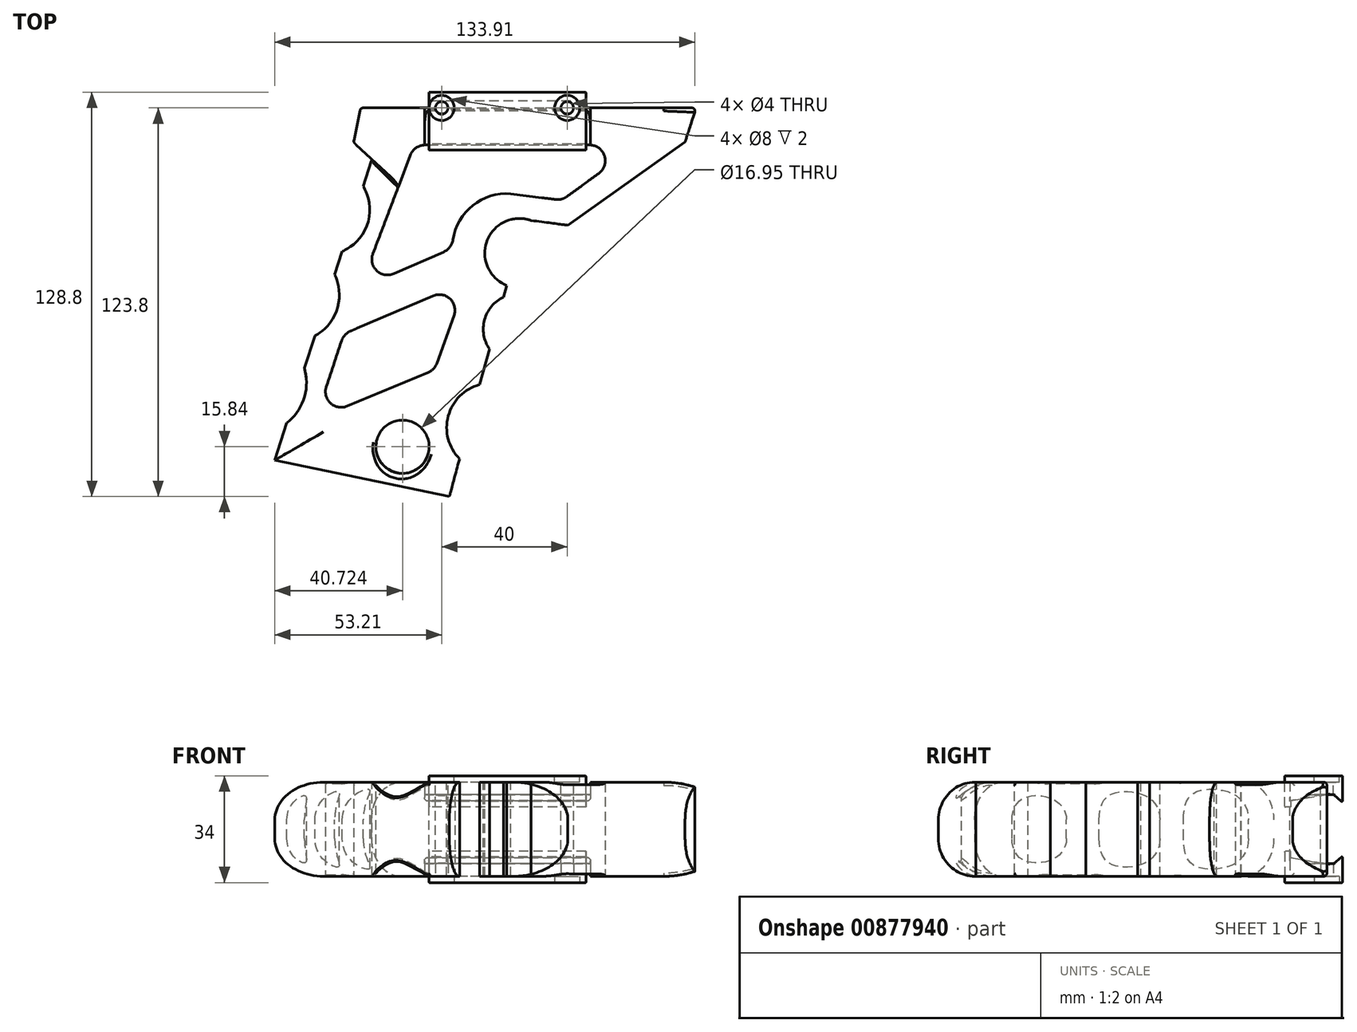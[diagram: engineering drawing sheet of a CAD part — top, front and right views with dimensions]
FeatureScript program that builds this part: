
annotation { "Feature Type Name" : "Feature", "Feature Type Description" : "" }
export const myFeature = defineFeature(function(context is Context, id is Id, definition is map)
    precondition{}
    {
        {
            var Q0;
            Q0=qCreatedBy(makeId("Top.planeOp"),FACE);
            var sketch = newSketch(context, id + "F0", { "sketchPlane" : qUnion([Q0])});
            skLineSegment(sketch, "E0", {"start": v(-36.24, 0) * mm, "end": v(-38.5, -10.92) * mm});
            skLineSegment(sketch, "E1", {"start": v(-38.5, -10.92) * mm, "end": v(-32.62, -16.35) * mm});
            skLineSegment(sketch, "E2", {"start": v(-32.62, -16.35) * mm, "end": v(-63.6, -112.26) * mm});
            skLineSegment(sketch, "E3", {"start": v(-63.6, -112.26) * mm, "end": v(-7.96, -123.8) * mm});
            skLineSegment(sketch, "E4", {"start": v(-7.96, -123.8) * mm, "end": v(16.02, -35.58) * mm});
            skLineSegment(sketch, "E5", {"start": v(16.02, -35.58) * mm, "end": v(29.82, -37.39) * mm});
            skLineSegment(sketch, "E6", {"start": v(29.82, -37.39) * mm, "end": v(67.14, -10.92) * mm});
            skLineSegment(sketch, "E7", {"start": v(67.14, -10.92) * mm, "end": v(70.67, 0) * mm});
            skLineSegment(sketch, "E8", {"start": v(-36.24, 0) * mm, "end": v(70.67, 0) * mm});
            skPoint(sketch, "E9.first.point", {"position": v(-35.48, -25.23) * mm});
            skPoint(sketch, "E9.second.point", {"position": v(-42.4, -46.63) * mm});
            skPoint(sketch, "E9.third.point", {"position": v(-65.03, -33.08) * mm});
            skPoint(sketch, "E10.first.point", {"position": v(-44.67, -53.65) * mm});
            skPoint(sketch, "E10.second.point", {"position": v(-50.9, -72.91) * mm});
            skPoint(sketch, "E10.third.point", {"position": v(-72.52, -56.97) * mm});
            skPoint(sketch, "E11.first.point", {"position": v(-54.13, -82.94) * mm});
            skPoint(sketch, "E11.second.point", {"position": v(-59.89, -100.75) * mm});
            skPoint(sketch, "E11.third.point", {"position": v(-85, -82.64) * mm});
            skLineSegment(sketch, "E12", {"start": v(-97.37, -25.23) * mm, "end": v(-7.02, -25.23) * mm, "construction": true});
            skLineSegment(sketch, "E13", {"start": v(-95.85, -46.63) * mm, "end": v(-7.4, -46.63) * mm, "construction": true});
            skLineSegment(sketch, "E14", {"start": v(-81.01, -53.65) * mm, "end": v(-12.15, -53.65) * mm, "construction": true});
            skLineSegment(sketch, "E15", {"start": v(-92.8, -72.91) * mm, "end": v(-15.2, -72.91) * mm, "construction": true});
            skLineSegment(sketch, "E16", {"start": v(-54.13, -82.94) * mm, "end": v(-73.21, -82.94) * mm});
            skLineSegment(sketch, "E17", {"start": v(-73.21, -82.94) * mm, "end": v(-28.9, -82.94) * mm, "construction": true});
            skLineSegment(sketch, "E18", {"start": v(-59.89, -100.75) * mm, "end": v(-91.1, -100.75) * mm});
            skLineSegment(sketch, "E19", {"start": v(-91.1, -100.75) * mm, "end": v(-23.57, -100.75) * mm, "construction": true});
            skLineSegment(sketch, "E20", {"start": v(-30.41, -25.23) * mm, "end": v(-60.21, -112.97) * mm, "construction": true});
            skSolve(sketch);
        }
        {
            var Q0;
            Q0 = qSketchRegion(id + "F0", true);
            extrude(context, id + "F1", {"entities" : qUnion([Q0]), "endBound" : BoundingType.SYMMETRIC, "depth" : 30 * mm, "offsetDistance" : 25 * mm});
        }
        {
            var Q0;
            Q0=qCreatedBy(makeId("Top.planeOp"),FACE);
            var sketch = newSketch(context, id + "F2", { "sketchPlane" : qUnion([Q0])});
            skCircle(sketch, "E21", {"center": v(-47.66, -32.46) * mm, "radius": 14.36 * mm});
            skPoint(sketch, "E21.first.point", {"position": v(-35.59, -24.68) * mm});
            skPoint(sketch, "E21.second.point", {"position": v(-43.3, -46.15) * mm});
            skPoint(sketch, "E21.third.point", {"position": v(-61.39, -28.25) * mm});
            skCircle(sketch, "E22", {"center": v(-57.68, -59.62) * mm, "radius": 14.67 * mm});
            skPoint(sketch, "E22.first.point", {"position": v(-44.44, -53.3) * mm});
            skPoint(sketch, "E22.second.point", {"position": v(-51.03, -72.7) * mm});
            skPoint(sketch, "E22.third.point", {"position": v(-72.31, -58.58) * mm});
            skCircle(sketch, "E23", {"center": v(-69.65, -87.55) * mm, "radius": 16.16 * mm});
            skPoint(sketch, "E23.first.point", {"position": v(-54.23, -82.68) * mm});
            skPoint(sketch, "E23.second.point", {"position": v(-60.07, -100.57) * mm});
            skPoint(sketch, "E23.third.point", {"position": v(-85.5, -84.38) * mm});
            skCircle(sketch, "E24", {"center": v(-22.89, -107.96) * mm, "radius": 8.48 * mm});
            skPoint(sketch, "E24.first.point", {"position": v(-24.85, -116.2) * mm});
            skPoint(sketch, "E24.second.point", {"position": v(-20.52, -99.82) * mm});
            skPoint(sketch, "E24.third.point", {"position": v(-15.62, -103.59) * mm});
            skCircle(sketch, "E25", {"center": v(14.39, -46.27) * mm, "radius": 11.05 * mm});
            skPoint(sketch, "E25.first.point", {"position": v(16.03, -35.34) * mm});
            skPoint(sketch, "E25.second.point", {"position": v(10.2, -56.5) * mm});
            skPoint(sketch, "E25.third.point", {"position": v(23.76, -52.13) * mm});
            skCircle(sketch, "E26", {"center": v(14.16, -70.47) * mm, "radius": 11.31 * mm});
            skPoint(sketch, "E26.first.point", {"position": v(9.42, -60.2) * mm});
            skPoint(sketch, "E26.second.point", {"position": v(5.17, -77.33) * mm});
            skPoint(sketch, "E26.third.point", {"position": v(24.99, -73.75) * mm});
            skCircle(sketch, "E27", {"center": v(5.4, -101.86) * mm, "radius": 14.2 * mm});
            skPoint(sketch, "E27.first.point", {"position": v(2, -88.08) * mm});
            skPoint(sketch, "E27.second.point", {"position": v(-4.5, -112.05) * mm});
            skPoint(sketch, "E27.third.point", {"position": v(18.9, -106.22) * mm});
            skSolve(sketch);
        }
        {
            var Q0;
            Q0 = qSketchRegion(id + "F2", true);
            extrude(context, id + "F3", {"entities" : qUnion([Q0]), "operationType" : NewBodyOperationType.REMOVE, "endBound" : BoundingType.SYMMETRIC, "oppositeDirection" : true, "depth" : 30 * mm, "offsetDistance" : 25 * mm});
        }
        {
            var Q0;
            {var subQ0=sQuery(id+"F2.wireOp",EDGE,"E22");Q0=makeQuery(id+"F3.boolean.opBoolean","COPY",EDGE,{"derivedFrom":makeQuery(id+"F3.opExtrude","CAP_EDGE",EDGE,{"disambiguationData":[OSD([subQ0]),TDD([makeQuery(id+"F2.imprint","IMPRINT",EDGE,{"disambiguationData":[TD([[makeQuery(id+"F2.imprint","INTERSECT",VERTEX,{"disambiguationData":[OD(1.0)],"derivedFrom":[sQuery(id+"F2.wireOp",EDGE,"E21"),subQ0]}),1.0]])],"derivedFrom":subQ0})])],"isStart":true})});}
            var Q1;
            Q1=makeQuery(id+"F3.boolean.opBoolean","COPY",EDGE,{"derivedFrom":makeQuery(id+"F3.opExtrude","CAP_EDGE",EDGE,{"disambiguationData":[OSD([sQuery(id+"F2.wireOp",EDGE,"E21")])],"isStart":true})});
            var Q2;
            Q2=makeQuery(id+"F3.boolean.opBoolean","COPY",EDGE,{"derivedFrom":makeQuery(id+"F3.opExtrude","CAP_EDGE",EDGE,{"disambiguationData":[OSD([sQuery(id+"F2.wireOp",EDGE,"E23")])],"isStart":true})});
            var Q3;
            Q3=makeQuery(id+"F3.boolean.opBoolean","COPY",EDGE,{"derivedFrom":makeQuery(id+"F3.opExtrude","CAP_EDGE",EDGE,{"disambiguationData":[OSD([sQuery(id+"F2.wireOp",EDGE,"E21")])],"isStart":false})});
            var Q4;
            {var subQ0=sQuery(id+"F2.wireOp",EDGE,"E22");Q4=makeQuery(id+"F3.boolean.opBoolean","COPY",EDGE,{"derivedFrom":makeQuery(id+"F3.opExtrude","CAP_EDGE",EDGE,{"disambiguationData":[OSD([subQ0]),TDD([makeQuery(id+"F2.imprint","IMPRINT",EDGE,{"disambiguationData":[TD([[makeQuery(id+"F2.imprint","INTERSECT",VERTEX,{"disambiguationData":[OD(1.0)],"derivedFrom":[sQuery(id+"F2.wireOp",EDGE,"E21"),subQ0]}),1.0]])],"derivedFrom":subQ0})])],"isStart":false})});}
            var Q5;
            Q5=makeQuery(id+"F3.boolean.opBoolean","COPY",EDGE,{"derivedFrom":makeQuery(id+"F3.opExtrude","CAP_EDGE",EDGE,{"disambiguationData":[OSD([sQuery(id+"F2.wireOp",EDGE,"E23")])],"isStart":false})});
            var Q6;
            {var subQ0=sQuery(id+"F0.wireOp",EDGE,"E2");var subQ1=sQuery(id+"F2.wireOp",EDGE,"E22");var subQ2=sQuery(id+"F2.wireOp",EDGE,"E23");Q6=makeQuery(id+"F3.boolean.opBoolean","SPLIT",EDGE,{"disambiguationData":[TD([makeQuery(id+"F1.opExtrude","CAP_FACE",FACE,{"disambiguationData":[OSD([sQuery(id+"F0.wireOp",EDGE,"E0"),sQuery(id+"F0.wireOp",EDGE,"E1"),subQ0,sQuery(id+"F0.wireOp",EDGE,"E3"),sQuery(id+"F0.wireOp",EDGE,"E4"),sQuery(id+"F0.wireOp",EDGE,"E5"),sQuery(id+"F0.wireOp",EDGE,"E6"),sQuery(id+"F0.wireOp",EDGE,"E7"),sQuery(id+"F0.wireOp",EDGE,"E8")])],"isStart":false}),makeQuery(id+"F1.opExtrude","SWEPT_FACE",FACE,{"disambiguationData":[OSD([subQ0])]}),makeQuery(id+"F3.opExtrude","SWEPT_FACE",FACE,{"disambiguationData":[OSD([subQ1]),TDD([makeQuery(id+"F2.imprint","IMPRINT",EDGE,{"disambiguationData":[TD([[makeQuery(id+"F2.imprint","INTERSECT",VERTEX,{"disambiguationData":[OD(1.0)],"derivedFrom":[sQuery(id+"F2.wireOp",EDGE,"E21"),subQ1]}),1.0]])],"derivedFrom":subQ1})])]}),makeQuery(id+"F3.opExtrude","SWEPT_FACE",FACE,{"disambiguationData":[OSD([subQ2])]})])],"derivedFrom":makeQuery(id+"F1.opExtrude","CAP_EDGE",EDGE,{"disambiguationData":[OSD([subQ0])],"isStart":false})});}
            var Q7;
            {var subQ0=sQuery(id+"F0.wireOp",EDGE,"E2");var subQ1=sQuery(id+"F2.wireOp",EDGE,"E22");var subQ2=sQuery(id+"F2.wireOp",EDGE,"E21");Q7=makeQuery(id+"F3.boolean.opBoolean","SPLIT",EDGE,{"disambiguationData":[TD([makeQuery(id+"F1.opExtrude","CAP_FACE",FACE,{"disambiguationData":[OSD([sQuery(id+"F0.wireOp",EDGE,"E0"),sQuery(id+"F0.wireOp",EDGE,"E1"),subQ0,sQuery(id+"F0.wireOp",EDGE,"E3"),sQuery(id+"F0.wireOp",EDGE,"E4"),sQuery(id+"F0.wireOp",EDGE,"E5"),sQuery(id+"F0.wireOp",EDGE,"E6"),sQuery(id+"F0.wireOp",EDGE,"E7"),sQuery(id+"F0.wireOp",EDGE,"E8")])],"isStart":false}),makeQuery(id+"F1.opExtrude","SWEPT_FACE",FACE,{"disambiguationData":[OSD([subQ0])]}),makeQuery(id+"F3.opExtrude","SWEPT_FACE",FACE,{"disambiguationData":[OSD([subQ2])]}),makeQuery(id+"F3.opExtrude","SWEPT_FACE",FACE,{"disambiguationData":[OSD([subQ1]),TDD([makeQuery(id+"F2.imprint","IMPRINT",EDGE,{"disambiguationData":[TD([[makeQuery(id+"F2.imprint","INTERSECT",VERTEX,{"disambiguationData":[OD(1.0)],"derivedFrom":[subQ2,subQ1]}),1.0]])],"derivedFrom":subQ1})])]})])],"derivedFrom":makeQuery(id+"F1.opExtrude","CAP_EDGE",EDGE,{"disambiguationData":[OSD([subQ0])],"isStart":false})});}
            var Q8;
            {var subQ0=sQuery(id+"F0.wireOp",EDGE,"E2");var subQ1=sQuery(id+"F2.wireOp",EDGE,"E22");var subQ2=sQuery(id+"F2.wireOp",EDGE,"E23");Q8=makeQuery(id+"F3.boolean.opBoolean","SPLIT",EDGE,{"disambiguationData":[TD([makeQuery(id+"F1.opExtrude","CAP_FACE",FACE,{"disambiguationData":[OSD([sQuery(id+"F0.wireOp",EDGE,"E0"),sQuery(id+"F0.wireOp",EDGE,"E1"),subQ0,sQuery(id+"F0.wireOp",EDGE,"E3"),sQuery(id+"F0.wireOp",EDGE,"E4"),sQuery(id+"F0.wireOp",EDGE,"E5"),sQuery(id+"F0.wireOp",EDGE,"E6"),sQuery(id+"F0.wireOp",EDGE,"E7"),sQuery(id+"F0.wireOp",EDGE,"E8")])],"isStart":true}),makeQuery(id+"F1.opExtrude","SWEPT_FACE",FACE,{"disambiguationData":[OSD([subQ0])]}),makeQuery(id+"F3.opExtrude","SWEPT_FACE",FACE,{"disambiguationData":[OSD([subQ1]),TDD([makeQuery(id+"F2.imprint","IMPRINT",EDGE,{"disambiguationData":[TD([[makeQuery(id+"F2.imprint","INTERSECT",VERTEX,{"disambiguationData":[OD(1.0)],"derivedFrom":[sQuery(id+"F2.wireOp",EDGE,"E21"),subQ1]}),1.0]])],"derivedFrom":subQ1})])]}),makeQuery(id+"F3.opExtrude","SWEPT_FACE",FACE,{"disambiguationData":[OSD([subQ2])]})])],"derivedFrom":makeQuery(id+"F1.opExtrude","CAP_EDGE",EDGE,{"disambiguationData":[OSD([subQ0])],"isStart":true})});}
            var Q9;
            {var subQ0=sQuery(id+"F0.wireOp",EDGE,"E2");var subQ1=sQuery(id+"F2.wireOp",EDGE,"E21");var subQ2=sQuery(id+"F2.wireOp",EDGE,"E22");Q9=makeQuery(id+"F3.boolean.opBoolean","SPLIT",EDGE,{"disambiguationData":[TD([makeQuery(id+"F1.opExtrude","CAP_FACE",FACE,{"disambiguationData":[OSD([sQuery(id+"F0.wireOp",EDGE,"E0"),sQuery(id+"F0.wireOp",EDGE,"E1"),subQ0,sQuery(id+"F0.wireOp",EDGE,"E3"),sQuery(id+"F0.wireOp",EDGE,"E4"),sQuery(id+"F0.wireOp",EDGE,"E5"),sQuery(id+"F0.wireOp",EDGE,"E6"),sQuery(id+"F0.wireOp",EDGE,"E7"),sQuery(id+"F0.wireOp",EDGE,"E8")])],"isStart":true}),makeQuery(id+"F1.opExtrude","SWEPT_FACE",FACE,{"disambiguationData":[OSD([subQ0])]}),makeQuery(id+"F3.opExtrude","SWEPT_FACE",FACE,{"disambiguationData":[OSD([subQ1])]}),makeQuery(id+"F3.opExtrude","SWEPT_FACE",FACE,{"disambiguationData":[OSD([subQ2]),TDD([makeQuery(id+"F2.imprint","IMPRINT",EDGE,{"disambiguationData":[TD([[makeQuery(id+"F2.imprint","INTERSECT",VERTEX,{"disambiguationData":[OD(1.0)],"derivedFrom":[subQ1,subQ2]}),1.0]])],"derivedFrom":subQ2})])]})])],"derivedFrom":makeQuery(id+"F1.opExtrude","CAP_EDGE",EDGE,{"disambiguationData":[OSD([subQ0])],"isStart":true})});}
            var Q10;
            Q10=makeQuery(id+"F3.boolean.opBoolean","COPY",EDGE,{"derivedFrom":makeQuery(id+"F3.opExtrude","CAP_EDGE",EDGE,{"disambiguationData":[OSD([sQuery(id+"F2.wireOp",EDGE,"E25")])],"isStart":true})});
            var Q11;
            Q11=makeQuery(id+"F3.boolean.opBoolean","COPY",EDGE,{"derivedFrom":makeQuery(id+"F3.opExtrude","CAP_EDGE",EDGE,{"disambiguationData":[OSD([sQuery(id+"F2.wireOp",EDGE,"E26")])],"isStart":true})});
            var Q12;
            Q12=makeQuery(id+"F3.boolean.opBoolean","COPY",EDGE,{"derivedFrom":makeQuery(id+"F3.opExtrude","CAP_EDGE",EDGE,{"disambiguationData":[OSD([sQuery(id+"F2.wireOp",EDGE,"E27")])],"isStart":true})});
            var Q13;
            Q13=makeQuery(id+"F3.boolean.opBoolean","COPY",EDGE,{"derivedFrom":makeQuery(id+"F3.opExtrude","CAP_EDGE",EDGE,{"disambiguationData":[OSD([sQuery(id+"F2.wireOp",EDGE,"E27")])],"isStart":false})});
            var Q14;
            Q14=makeQuery(id+"F3.boolean.opBoolean","COPY",EDGE,{"derivedFrom":makeQuery(id+"F3.opExtrude","CAP_EDGE",EDGE,{"disambiguationData":[OSD([sQuery(id+"F2.wireOp",EDGE,"E26")])],"isStart":false})});
            var Q15;
            Q15=makeQuery(id+"F3.boolean.opBoolean","COPY",EDGE,{"derivedFrom":makeQuery(id+"F3.opExtrude","CAP_EDGE",EDGE,{"disambiguationData":[OSD([sQuery(id+"F2.wireOp",EDGE,"E25")])],"isStart":false})});
            var Q16;
            Q16=makeQuery(id+"F1.opExtrude","CAP_EDGE",EDGE,{"disambiguationData":[OSD([sQuery(id+"F0.wireOp",EDGE,"E6")])],"isStart":true});
            var Q17;
            Q17=makeQuery(id+"F1.opExtrude","CAP_EDGE",EDGE,{"disambiguationData":[OSD([sQuery(id+"F0.wireOp",EDGE,"E6")])],"isStart":false});
            var Q18;
            Q18=makeQuery(id+"F1.opExtrude","CAP_EDGE",EDGE,{"disambiguationData":[OSD([sQuery(id+"F0.wireOp",EDGE,"E3")])],"isStart":true});
            var Q19;
            Q19=makeQuery(id+"F1.opExtrude","CAP_EDGE",EDGE,{"disambiguationData":[OSD([sQuery(id+"F0.wireOp",EDGE,"E3")])],"isStart":false});
            fillet(context, id + "F4", {"entities" : qUnion([Q0, Q1, Q2, Q3, Q4, Q5, Q6, Q7, Q8, Q9, Q10, Q11, Q12, Q13, Q14, Q15, Q16, Q17, Q18, Q19]), "radius" : 12 * mm, "tangentPropagation" : true, "allowEdgeOverflow" : false});
        }
        {
            var Q0;
            Q0=makeQuery(id+"F1.opExtrude","SWEPT_EDGE",EDGE,{"disambiguationData":[OSD([sQuery(id+"F0.wireOp",EDGE,"E1"),sQuery(id+"F0.wireOp",EDGE,"E2")])]});
            var Q1;
            Q1=makeQuery(id+"F1.opExtrude","SWEPT_EDGE",EDGE,{"disambiguationData":[OSD([sQuery(id+"F0.wireOp",EDGE,"E0"),sQuery(id+"F0.wireOp",EDGE,"E1")])]});
            var Q2;
            Q2=makeQuery(id+"F1.opExtrude","SWEPT_EDGE",EDGE,{"disambiguationData":[OSD([sQuery(id+"F0.wireOp",EDGE,"E0"),sQuery(id+"F0.wireOp",EDGE,"E8")])]});
            var Q3;
            Q3=makeQuery(id+"F1.opExtrude","SWEPT_EDGE",EDGE,{"disambiguationData":[OSD([sQuery(id+"F0.wireOp",EDGE,"E7"),sQuery(id+"F0.wireOp",EDGE,"E8")])]});
            var Q4;
            Q4=makeQuery(id+"F1.opExtrude","CAP_EDGE",EDGE,{"disambiguationData":[OSD([sQuery(id+"F0.wireOp",EDGE,"E8")])],"isStart":false});
            var Q5;
            Q5=makeQuery(id+"F1.opExtrude","CAP_EDGE",EDGE,{"disambiguationData":[OSD([sQuery(id+"F0.wireOp",EDGE,"E8")])],"isStart":true});
            var Q6;
            Q6=makeQuery(id+"F1.opExtrude","CAP_EDGE",EDGE,{"disambiguationData":[OSD([sQuery(id+"F0.wireOp",EDGE,"E0")])],"isStart":false});
            var Q7;
            Q7=makeQuery(id+"F1.opExtrude","CAP_EDGE",EDGE,{"disambiguationData":[OSD([sQuery(id+"F0.wireOp",EDGE,"E0")])],"isStart":true});
            fillet(context, id + "F5", {"entities" : qUnion([Q0, Q1, Q2, Q3, Q4, Q5, Q6, Q7]), "radius" : 1 * mm, "tangentPropagation" : true, "allowEdgeOverflow" : false});
        }
        {
            var Q0;
            Q0=qCreatedBy(makeId("Top.planeOp"),FACE);
            var sketch = newSketch(context, id + "F6", { "sketchPlane" : qUnion([Q0])});
            skLineSegment(sketch, "E28", {"start": v(-50.63, -99.24) * mm, "end": v(-41.6, -72.02) * mm});
            skLineSegment(sketch, "E29", {"start": v(-41.6, -72.02) * mm, "end": v(-2.6, -55.36) * mm});
            skLineSegment(sketch, "E30", {"start": v(-2.6, -55.36) * mm, "end": v(-12.68, -83.42) * mm});
            skLineSegment(sketch, "E31", {"start": v(-12.68, -83.42) * mm, "end": v(-50.63, -99.24) * mm});
            skLineSegment(sketch, "E32", {"start": v(-36.57, -57.58) * mm, "end": v(-19.15, -11.81) * mm});
            skLineSegment(sketch, "E33", {"start": v(-19.15, -11.81) * mm, "end": v(52.14, -11.81) * mm});
            skLineSegment(sketch, "E34", {"start": v(52.14, -11.81) * mm, "end": v(27.84, -29.42) * mm});
            skLineSegment(sketch, "E35", {"start": v(27.84, -29.42) * mm, "end": v(11.65, -27.35) * mm});
            skLineSegment(sketch, "E36", {"start": v(-36.57, -57.58) * mm, "end": v(-7, -44.68) * mm});
            skArc(sketch, "E37", {"start": v(13.34, -27.57) * mm, "mid": v(-0.83, -31.36) * mm, "end": v(-7, -44.68) * mm});
            skPoint(sketch, "E37.third.point", {"position": v(24.64, -54.28) * mm});
            skSolve(sketch);
        }
        {
            var Q0;
            Q0 = qSketchRegion(id + "F6", true);
            extrude(context, id + "F7", {"entities" : qUnion([Q0]), "operationType" : NewBodyOperationType.REMOVE, "endBound" : BoundingType.SYMMETRIC, "oppositeDirection" : true, "depth" : 30 * mm, "offsetDistance" : 25 * mm});
        }
        {
            var Q0;
            Q0=makeQuery(id+"F4.opFillet","BLEND_EDGE",EDGE,{"blendedFrom":[makeQuery(id+"F1.opExtrude","CAP_EDGE",EDGE,{"disambiguationData":[OSD([sQuery(id+"F0.wireOp",EDGE,"E3")])],"isStart":false}),makeQuery(id+"F3.boolean.opBoolean","COPY",FACE,{"derivedFrom":makeQuery(id+"F3.opExtrude","SWEPT_FACE",FACE,{"disambiguationData":[OSD([sQuery(id+"F2.wireOp",EDGE,"E24")])]})})],"blendedInto":[makeQuery(id+"F3.boolean.opBoolean","COPY",FACE,{"derivedFrom":makeQuery(id+"F3.opExtrude","SWEPT_FACE",FACE,{"disambiguationData":[OSD([sQuery(id+"F2.wireOp",EDGE,"E24")])]})})]});
            var Q1;
            Q1=makeQuery(id+"F4.opFillet","BLEND_EDGE",EDGE,{"blendedFrom":[makeQuery(id+"F1.opExtrude","CAP_EDGE",EDGE,{"disambiguationData":[OSD([sQuery(id+"F0.wireOp",EDGE,"E3")])],"isStart":true}),makeQuery(id+"F3.boolean.opBoolean","COPY",FACE,{"derivedFrom":makeQuery(id+"F3.opExtrude","SWEPT_FACE",FACE,{"disambiguationData":[OSD([sQuery(id+"F2.wireOp",EDGE,"E24")])]})})],"blendedInto":[makeQuery(id+"F3.boolean.opBoolean","COPY",FACE,{"derivedFrom":makeQuery(id+"F3.opExtrude","SWEPT_FACE",FACE,{"disambiguationData":[OSD([sQuery(id+"F2.wireOp",EDGE,"E24")])]})})]});
            fillet(context, id + "F8", {"entities" : qUnion([Q0, Q1]), "radius" : 1 * mm, "tangentPropagation" : true, "allowEdgeOverflow" : false});
        }
        {
            var Q0;
            Q0=makeQuery(id+"F7.boolean.opBoolean","COPY",EDGE,{"derivedFrom":makeQuery(id+"F7.opExtrude","SWEPT_EDGE",EDGE,{"disambiguationData":[OSD([sQuery(id+"F6.wireOp",EDGE,"E28"),sQuery(id+"F6.wireOp",EDGE,"E31")])]})});
            var Q1;
            Q1=makeQuery(id+"F7.boolean.opBoolean","COPY",EDGE,{"derivedFrom":makeQuery(id+"F7.opExtrude","SWEPT_EDGE",EDGE,{"disambiguationData":[OSD([sQuery(id+"F6.wireOp",EDGE,"E29"),sQuery(id+"F6.wireOp",EDGE,"E30")])]})});
            var Q2;
            Q2=makeQuery(id+"F7.boolean.opBoolean","COPY",EDGE,{"derivedFrom":makeQuery(id+"F7.opExtrude","SWEPT_EDGE",EDGE,{"disambiguationData":[OSD([sQuery(id+"F6.wireOp",EDGE,"E28"),sQuery(id+"F6.wireOp",EDGE,"E29")])]})});
            var Q3;
            Q3=makeQuery(id+"F7.boolean.opBoolean","COPY",EDGE,{"derivedFrom":makeQuery(id+"F7.opExtrude","SWEPT_EDGE",EDGE,{"disambiguationData":[OSD([sQuery(id+"F6.wireOp",EDGE,"E30"),sQuery(id+"F6.wireOp",EDGE,"E31")])]})});
            var Q4;
            Q4=makeQuery(id+"F7.boolean.opBoolean","COPY",EDGE,{"derivedFrom":makeQuery(id+"F7.opExtrude","SWEPT_EDGE",EDGE,{"disambiguationData":[OSD([sQuery(id+"F6.wireOp",EDGE,"E32"),sQuery(id+"F6.wireOp",EDGE,"E36")])]})});
            var Q5;
            Q5=makeQuery(id+"F7.boolean.opBoolean","COPY",EDGE,{"derivedFrom":makeQuery(id+"F7.opExtrude","SWEPT_EDGE",EDGE,{"disambiguationData":[OSD([sQuery(id+"F6.wireOp",EDGE,"E32"),sQuery(id+"F6.wireOp",EDGE,"E33")])]})});
            var Q6;
            Q6=makeQuery(id+"F7.boolean.opBoolean","COPY",EDGE,{"derivedFrom":makeQuery(id+"F7.opExtrude","SWEPT_EDGE",EDGE,{"disambiguationData":[OSD([sQuery(id+"F6.wireOp",EDGE,"E33"),sQuery(id+"F6.wireOp",EDGE,"E34")])]})});
            var Q7;
            Q7=makeQuery(id+"F7.boolean.opBoolean","COPY",EDGE,{"derivedFrom":makeQuery(id+"F7.opExtrude","SWEPT_EDGE",EDGE,{"disambiguationData":[OSD([sQuery(id+"F6.wireOp",EDGE,"E34"),sQuery(id+"F6.wireOp",EDGE,"E35")])]})});
            var Q8;
            Q8=makeQuery(id+"F7.boolean.opBoolean","COPY",EDGE,{"derivedFrom":makeQuery(id+"F7.opExtrude","SWEPT_EDGE",EDGE,{"disambiguationData":[OSD([sQuery(id+"F6.wireOp",EDGE,"E36"),sQuery(id+"F6.wireOp",EDGE,"E37")])]})});
            fillet(context, id + "F9", {"entities" : qUnion([Q0, Q1, Q2, Q3, Q4, Q5, Q6, Q7, Q8]), "radius" : 5 * mm, "tangentPropagation" : true, "allowEdgeOverflow" : false});
        }
        {
            var Q0;
            Q0=qCreatedBy(makeId("Right.planeOp"),FACE);
            var sketch = newSketch(context, id + "F10", { "sketchPlane" : qUnion([Q0])});
            skLineSegment(sketch, "E38", {"start": v(-1, 11) * mm, "end": v(-11.96, 9.07) * mm});
            skLineSegment(sketch, "E39", {"start": v(-11.96, 13.97) * mm, "end": v(-11.96, 9.07) * mm});
            skLineSegment(sketch, "E40", {"start": v(0, 0) * mm, "end": v(-125.67, 0) * mm, "construction": true});
            skLineSegment(sketch, "E41.MirrorCS", {"start": v(-1, -11) * mm, "end": v(-11.96, -9.07) * mm});
            skLineSegment(sketch, "E42.MirrorCS", {"start": v(-1, -17.8) * mm, "end": v(-11.96, -17.8) * mm});
            skLineSegment(sketch, "E43.MirrorCS", {"start": v(-11.96, -17.8) * mm, "end": v(-11.96, -9.07) * mm});
            skLineSegment(sketch, "E44.top", {"start": v(-1, 11) * mm, "end": v(1.5, 11) * mm});
            skLineSegment(sketch, "E44.right", {"start": v(1.5, 13.97) * mm, "end": v(1.5, 11) * mm});
            skLineSegment(sketch, "E45.bottom", {"start": v(-1, -11) * mm, "end": v(1.5, -11) * mm});
            skLineSegment(sketch, "E45.top", {"start": v(-1, -17.8) * mm, "end": v(1.5, -17.8) * mm});
            skLineSegment(sketch, "E45.right", {"start": v(1.5, -11) * mm, "end": v(1.5, -17.8) * mm});
            skLineSegment(sketch, "E46.top", {"start": v(-11.96, 17.3) * mm, "end": v(1.5, 17.3) * mm});
            skLineSegment(sketch, "E46.left", {"start": v(-11.96, 13.97) * mm, "end": v(-11.96, 17.3) * mm});
            skLineSegment(sketch, "E46.right", {"start": v(1.5, 13.97) * mm, "end": v(1.5, 17.3) * mm});
            skSolve(sketch);
        }
        {
            var Q0;
            Q0 = qSketchRegion(id + "F10", true);
            extrude(context, id + "F11", {"entities" : qUnion([Q0]), "operationType" : NewBodyOperationType.REMOVE, "depth" : 37 * mm, "offsetDistance" : 25 * mm, "hasSecondDirection" : true, "secondDirectionOppositeDirection" : true, "secondDirectionDepth" : 15.9 * mm});
        }
        {
            var Q0;
            Q0=makeQuery(id+"F11.boolean.opBoolean","COPY",EDGE,{"derivedFrom":makeQuery(id+"F11.opExtrude","CAP_EDGE",EDGE,{"disambiguationData":[OSD([sQuery(id+"F10.wireOp",EDGE,"E38")])],"isStart":true})});
            var Q1;
            Q1=makeQuery(id+"F11.boolean.opBoolean","COPY",EDGE,{"derivedFrom":makeQuery(id+"F11.opExtrude","CAP_EDGE",EDGE,{"disambiguationData":[OSD([sQuery(id+"F10.wireOp",EDGE,"E38")])],"isStart":false})});
            var Q2;
            Q2=makeQuery(id+"F11.boolean.opBoolean","COPY",EDGE,{"derivedFrom":makeQuery(id+"F11.opExtrude","CAP_EDGE",EDGE,{"disambiguationData":[OSD([sQuery(id+"F10.wireOp",EDGE,"E41.MirrorCS")])],"isStart":false})});
            var Q3;
            Q3=makeQuery(id+"F11.boolean.opBoolean","COPY",EDGE,{"derivedFrom":makeQuery(id+"F11.opExtrude","CAP_EDGE",EDGE,{"disambiguationData":[OSD([sQuery(id+"F10.wireOp",EDGE,"E41.MirrorCS")])],"isStart":true})});
            fillet(context, id + "F12", {"entities" : qUnion([Q0, Q1, Q2, Q3]), "radius" : 1 * mm, "tangentPropagation" : true, "allowEdgeOverflow" : false});
        }
        {
            var Q0;
            Q0=qCreatedBy(makeId("Right.planeOp"),FACE);
            var sketch = newSketch(context, id + "F13", { "sketchPlane" : qUnion([Q0])});
            skPoint(sketch, "E47", {"position": v(-11.48, 9.07) * mm});
            skPoint(sketch, "E48", {"position": v(-0.51, 11) * mm});
            skPoint(sketch, "E49", {"position": v(1.99, 11) * mm});
            skLineSegment(sketch, "E50", {"start": v(-11.48, 9.07) * mm, "end": v(-0.51, 11) * mm});
            skLineSegment(sketch, "E51", {"start": v(-11.48, 9.07) * mm, "end": v(-11.48, 7.07) * mm});
            skLineSegment(sketch, "E52", {"start": v(-11.48, 7.07) * mm, "end": v(-13.48, 7.07) * mm});
            skLineSegment(sketch, "E53", {"start": v(-13.48, 7.07) * mm, "end": v(-13.48, 17) * mm});
            skLineSegment(sketch, "E54", {"start": v(5, 11) * mm, "end": v(5, 17) * mm});
            skLineSegment(sketch, "E55", {"start": v(5, 17) * mm, "end": v(-13.48, 17) * mm});
            skLineSegment(sketch, "E56", {"start": v(5, 8.5) * mm, "end": v(5, 11) * mm});
            skLineSegment(sketch, "E57", {"start": v(2.24, 11) * mm, "end": v(5, 8.5) * mm});
            skLineSegment(sketch, "E58", {"start": v(-0.51, 11) * mm, "end": v(2.24, 11) * mm});
            skLineSegment(sketch, "E59.MirrorCS", {"start": v(-11.48, -7.07) * mm, "end": v(-13.48, -7.07) * mm});
            skLineSegment(sketch, "E60.MirrorCS", {"start": v(-11.48, -9.07) * mm, "end": v(-11.48, -7.07) * mm});
            skLineSegment(sketch, "E61.MirrorCS", {"start": v(-0.51, -11) * mm, "end": v(2.24, -11) * mm});
            skPoint(sketch, "E62.MirrorP", {"position": v(-11.48, -9.07) * mm});
            skLineSegment(sketch, "E63.MirrorCS", {"start": v(-11.48, -9.07) * mm, "end": v(-0.51, -11) * mm});
            skLineSegment(sketch, "E64.MirrorCS", {"start": v(5, -17) * mm, "end": v(-13.48, -17) * mm});
            skLineSegment(sketch, "E65.MirrorCS", {"start": v(5, -11) * mm, "end": v(5, -17) * mm});
            skPoint(sketch, "E66.MirrorP", {"position": v(1.99, -11) * mm});
            skLineSegment(sketch, "E67.MirrorCS", {"start": v(5, -8.5) * mm, "end": v(5, -11) * mm});
            skLineSegment(sketch, "E68.MirrorCS", {"start": v(2.24, -11) * mm, "end": v(5, -8.5) * mm});
            skLineSegment(sketch, "E69.MirrorCS", {"start": v(-13.48, -7.07) * mm, "end": v(-13.48, -17) * mm});
            skPoint(sketch, "E70.MirrorP", {"position": v(-0.51, -11) * mm});
            skSolve(sketch);
        }
        {
            var Q0;
            Q0 = qSketchRegion(id + "F13", true);
            extrude(context, id + "F14", {"entities" : qUnion([Q0]), "depth" : 35.6 * mm, "offsetDistance" : 25 * mm, "hasSecondDirection" : true, "secondDirectionOppositeDirection" : true, "secondDirectionDepth" : 14.5 * mm});
        }
        {
            var Q0;
            Q0=makeQuery(id+"F14.opExtrude","SWEPT_FACE",FACE,{"disambiguationData":[OSD([sQuery(id+"F13.wireOp",EDGE,"E55")])]});
            var sketch = newSketch(context, id + "F15", { "sketchPlane" : qUnion([Q0])});
            skPoint(sketch, "E71", {"position": v(29.6, 0) * mm});
            skPoint(sketch, "E72", {"position": v(-10.4, 0) * mm});
            skSolve(sketch);
        }
        {
            var Q0;
            Q0=sQuery(id+"F15.wireOp",VERTEX,"E71");
            var Q1;
            Q1=sQuery(id+"F15.wireOp",VERTEX,"E72");
            var Q2;
            Q2=makeQuery(id+"F14.opExtrude","SWEPT_BODY",BODY,{"disambiguationData":[OSD([sQuery(id+"F13.wireOp",EDGE,"E50"),sQuery(id+"F13.wireOp",EDGE,"E51"),sQuery(id+"F13.wireOp",EDGE,"E52"),sQuery(id+"F13.wireOp",EDGE,"E53"),sQuery(id+"F13.wireOp",EDGE,"E54"),sQuery(id+"F13.wireOp",EDGE,"E55"),sQuery(id+"F13.wireOp",EDGE,"E56"),sQuery(id+"F13.wireOp",EDGE,"E57"),sQuery(id+"F13.wireOp",EDGE,"E58")])]});
            var Q3;
            Q3=makeQuery(id+"F1.opExtrude","SWEPT_BODY",BODY,{"disambiguationData":[OSD([sQuery(id+"F0.wireOp",EDGE,"E0"),sQuery(id+"F0.wireOp",EDGE,"E1"),sQuery(id+"F0.wireOp",EDGE,"E2"),sQuery(id+"F0.wireOp",EDGE,"E3"),sQuery(id+"F0.wireOp",EDGE,"E4"),sQuery(id+"F0.wireOp",EDGE,"E5"),sQuery(id+"F0.wireOp",EDGE,"E6"),sQuery(id+"F0.wireOp",EDGE,"E7"),sQuery(id+"F0.wireOp",EDGE,"E8")])]});
            hole(context, id + "F16", {"style" : HoleStyle.C_BORE, "endStyle" : HoleEndStyle.BLIND, "holeDiameter" : 4 * mm, "cBoreDiameter" : 8 * mm, "cBoreDepth" : 2 * mm, "majorDiameter" : 5 * mm, "holeDepth" : 40 * mm, "isTappedThrough" : true, "tappedDepth" : 12 * mm, "tapClearance" : 3, "startFromSketch" : true, "locations" : qUnion([Q0, Q1]), "scope" : qUnion([Q2, Q3])});
        }
        {
            var Q0;
            Q0=makeQuery(id+"F14.opExtrude","SWEPT_EDGE",EDGE,{"disambiguationData":[OSD([sQuery(id+"F13.wireOp",EDGE,"E56"),sQuery(id+"F13.wireOp",EDGE,"E57")])]});
            var Q1;
            Q1=makeQuery(id+"F14.opExtrude","SWEPT_EDGE",EDGE,{"disambiguationData":[OSD([sQuery(id+"F13.wireOp",EDGE,"E67.MirrorCS"),sQuery(id+"F13.wireOp",EDGE,"E68.MirrorCS")])]});
            var Q2;
            Q2=makeQuery(id+"F14.opExtrude","SWEPT_EDGE",EDGE,{"disambiguationData":[OSD([sQuery(id+"F13.wireOp",EDGE,"E54"),sQuery(id+"F13.wireOp",EDGE,"E55")])]});
            var Q3;
            Q3=makeQuery(id+"F14.opExtrude","SWEPT_EDGE",EDGE,{"disambiguationData":[OSD([sQuery(id+"F13.wireOp",EDGE,"E64.MirrorCS"),sQuery(id+"F13.wireOp",EDGE,"E65.MirrorCS")])]});
            var Q4;
            Q4=makeQuery(id+"F14.opExtrude","CAP_EDGE",EDGE,{"disambiguationData":[OSD([sQuery(id+"F13.wireOp",EDGE,"E65.MirrorCS"),sQuery(id+"F13.wireOp",EDGE,"E67.MirrorCS")])],"isStart":false});
            var Q5;
            Q5=makeQuery(id+"F14.opExtrude","CAP_EDGE",EDGE,{"disambiguationData":[OSD([sQuery(id+"F13.wireOp",EDGE,"E65.MirrorCS"),sQuery(id+"F13.wireOp",EDGE,"E67.MirrorCS")])],"isStart":true});
            var Q6;
            Q6=makeQuery(id+"F14.opExtrude","CAP_EDGE",EDGE,{"disambiguationData":[OSD([sQuery(id+"F13.wireOp",EDGE,"E68.MirrorCS")])],"isStart":false});
            var Q7;
            Q7=makeQuery(id+"F14.opExtrude","CAP_EDGE",EDGE,{"disambiguationData":[OSD([sQuery(id+"F13.wireOp",EDGE,"E61.MirrorCS")])],"isStart":false});
            var Q8;
            Q8=makeQuery(id+"F14.opExtrude","CAP_EDGE",EDGE,{"disambiguationData":[OSD([sQuery(id+"F13.wireOp",EDGE,"E64.MirrorCS")])],"isStart":false});
            var Q9;
            Q9=makeQuery(id+"F14.opExtrude","CAP_EDGE",EDGE,{"disambiguationData":[OSD([sQuery(id+"F13.wireOp",EDGE,"E54"),sQuery(id+"F13.wireOp",EDGE,"E56")])],"isStart":false});
            var Q10;
            Q10=makeQuery(id+"F14.opExtrude","CAP_EDGE",EDGE,{"disambiguationData":[OSD([sQuery(id+"F13.wireOp",EDGE,"E57")])],"isStart":false});
            var Q11;
            Q11=makeQuery(id+"F14.opExtrude","CAP_EDGE",EDGE,{"disambiguationData":[OSD([sQuery(id+"F13.wireOp",EDGE,"E58")])],"isStart":false});
            var Q12;
            Q12=makeQuery(id+"F14.opExtrude","CAP_EDGE",EDGE,{"disambiguationData":[OSD([sQuery(id+"F13.wireOp",EDGE,"E55")])],"isStart":false});
            var Q13;
            Q13=makeQuery(id+"F14.opExtrude","CAP_EDGE",EDGE,{"disambiguationData":[OSD([sQuery(id+"F13.wireOp",EDGE,"E53")])],"isStart":false});
            var Q14;
            Q14=makeQuery(id+"F14.opExtrude","CAP_EDGE",EDGE,{"disambiguationData":[OSD([sQuery(id+"F13.wireOp",EDGE,"E55")])],"isStart":true});
            var Q15;
            Q15=makeQuery(id+"F14.opExtrude","CAP_EDGE",EDGE,{"disambiguationData":[OSD([sQuery(id+"F13.wireOp",EDGE,"E57")])],"isStart":true});
            var Q16;
            Q16=makeQuery(id+"F14.opExtrude","CAP_EDGE",EDGE,{"disambiguationData":[OSD([sQuery(id+"F13.wireOp",EDGE,"E58")])],"isStart":true});
            var Q17;
            Q17=makeQuery(id+"F14.opExtrude","SWEPT_EDGE",EDGE,{"disambiguationData":[OSD([sQuery(id+"F13.wireOp",EDGE,"E53"),sQuery(id+"F13.wireOp",EDGE,"E55")])]});
            var Q18;
            Q18=makeQuery(id+"F14.opExtrude","CAP_EDGE",EDGE,{"disambiguationData":[OSD([sQuery(id+"F13.wireOp",EDGE,"E53")])],"isStart":true});
            var Q19;
            Q19=makeQuery(id+"F14.opExtrude","SWEPT_EDGE",EDGE,{"disambiguationData":[OSD([sQuery(id+"F13.wireOp",EDGE,"E52"),sQuery(id+"F13.wireOp",EDGE,"E53")])]});
            var Q20;
            Q20=makeQuery(id+"F14.opExtrude","CAP_EDGE",EDGE,{"disambiguationData":[OSD([sQuery(id+"F13.wireOp",EDGE,"E64.MirrorCS")])],"isStart":true});
            var Q21;
            Q21=makeQuery(id+"F14.opExtrude","CAP_EDGE",EDGE,{"disambiguationData":[OSD([sQuery(id+"F13.wireOp",EDGE,"E68.MirrorCS")])],"isStart":true});
            var Q22;
            Q22=makeQuery(id+"F14.opExtrude","CAP_EDGE",EDGE,{"disambiguationData":[OSD([sQuery(id+"F13.wireOp",EDGE,"E61.MirrorCS")])],"isStart":true});
            var Q23;
            Q23=makeQuery(id+"F14.opExtrude","SWEPT_EDGE",EDGE,{"disambiguationData":[OSD([sQuery(id+"F13.wireOp",EDGE,"E64.MirrorCS"),sQuery(id+"F13.wireOp",EDGE,"E69.MirrorCS")])]});
            var Q24;
            Q24=makeQuery(id+"F14.opExtrude","CAP_EDGE",EDGE,{"disambiguationData":[OSD([sQuery(id+"F13.wireOp",EDGE,"E69.MirrorCS")])],"isStart":true});
            var Q25;
            Q25=makeQuery(id+"F14.opExtrude","SWEPT_EDGE",EDGE,{"disambiguationData":[OSD([sQuery(id+"F13.wireOp",EDGE,"E59.MirrorCS"),sQuery(id+"F13.wireOp",EDGE,"E69.MirrorCS")])]});
            var Q26;
            Q26=makeQuery(id+"F14.opExtrude","CAP_EDGE",EDGE,{"disambiguationData":[OSD([sQuery(id+"F13.wireOp",EDGE,"E69.MirrorCS")])],"isStart":false});
            fillet(context, id + "F17", {"entities" : qUnion([Q0, Q1, Q2, Q3, Q4, Q5, Q6, Q7, Q8, Q9, Q10, Q11, Q12, Q13, Q14, Q15, Q16, Q17, Q18, Q19, Q20, Q21, Q22, Q23, Q24, Q25, Q26]), "radius" : 0.25 * mm, "tangentPropagation" : true, "allowEdgeOverflow" : false});
        }
        {
            var Q0;
            Q0=makeQuery(id+"F14.opExtrude","SWEPT_FACE",FACE,{"disambiguationData":[OSD([sQuery(id+"F13.wireOp",EDGE,"E64.MirrorCS")])]});
            var sketch = newSketch(context, id + "F18", { "sketchPlane" : qUnion([Q0])});
            skPoint(sketch, "E73", {"position": v(-10.4, 0) * mm});
            skPoint(sketch, "E74", {"position": v(29.6, 0) * mm});
            skSolve(sketch);
        }
        {
            var Q0;
            Q0=sQuery(id+"F18.wireOp",VERTEX,"E73");
            var Q1;
            Q1=sQuery(id+"F18.wireOp",VERTEX,"E74");
            var Q2;
            Q2=makeQuery(id+"F14.opExtrude","SWEPT_BODY",BODY,{"disambiguationData":[OSD([sQuery(id+"F13.wireOp",EDGE,"E59.MirrorCS"),sQuery(id+"F13.wireOp",EDGE,"E60.MirrorCS"),sQuery(id+"F13.wireOp",EDGE,"E61.MirrorCS"),sQuery(id+"F13.wireOp",EDGE,"E63.MirrorCS"),sQuery(id+"F13.wireOp",EDGE,"E64.MirrorCS"),sQuery(id+"F13.wireOp",EDGE,"E65.MirrorCS"),sQuery(id+"F13.wireOp",EDGE,"E67.MirrorCS"),sQuery(id+"F13.wireOp",EDGE,"E68.MirrorCS"),sQuery(id+"F13.wireOp",EDGE,"E69.MirrorCS")])]});
            hole(context, id + "F19", {"style" : HoleStyle.C_BORE, "endStyle" : HoleEndStyle.BLIND, "holeDiameter" : 4 * mm, "cBoreDiameter" : 8 * mm, "cBoreDepth" : 2 * mm, "majorDiameter" : 5 * mm, "holeDepth" : 6.2 * mm, "isTappedThrough" : true, "tappedDepth" : 12 * mm, "tapClearance" : 3, "startFromSketch" : true, "locations" : qUnion([Q0, Q1]), "scope" : qUnion([Q2])});
        }
    });
